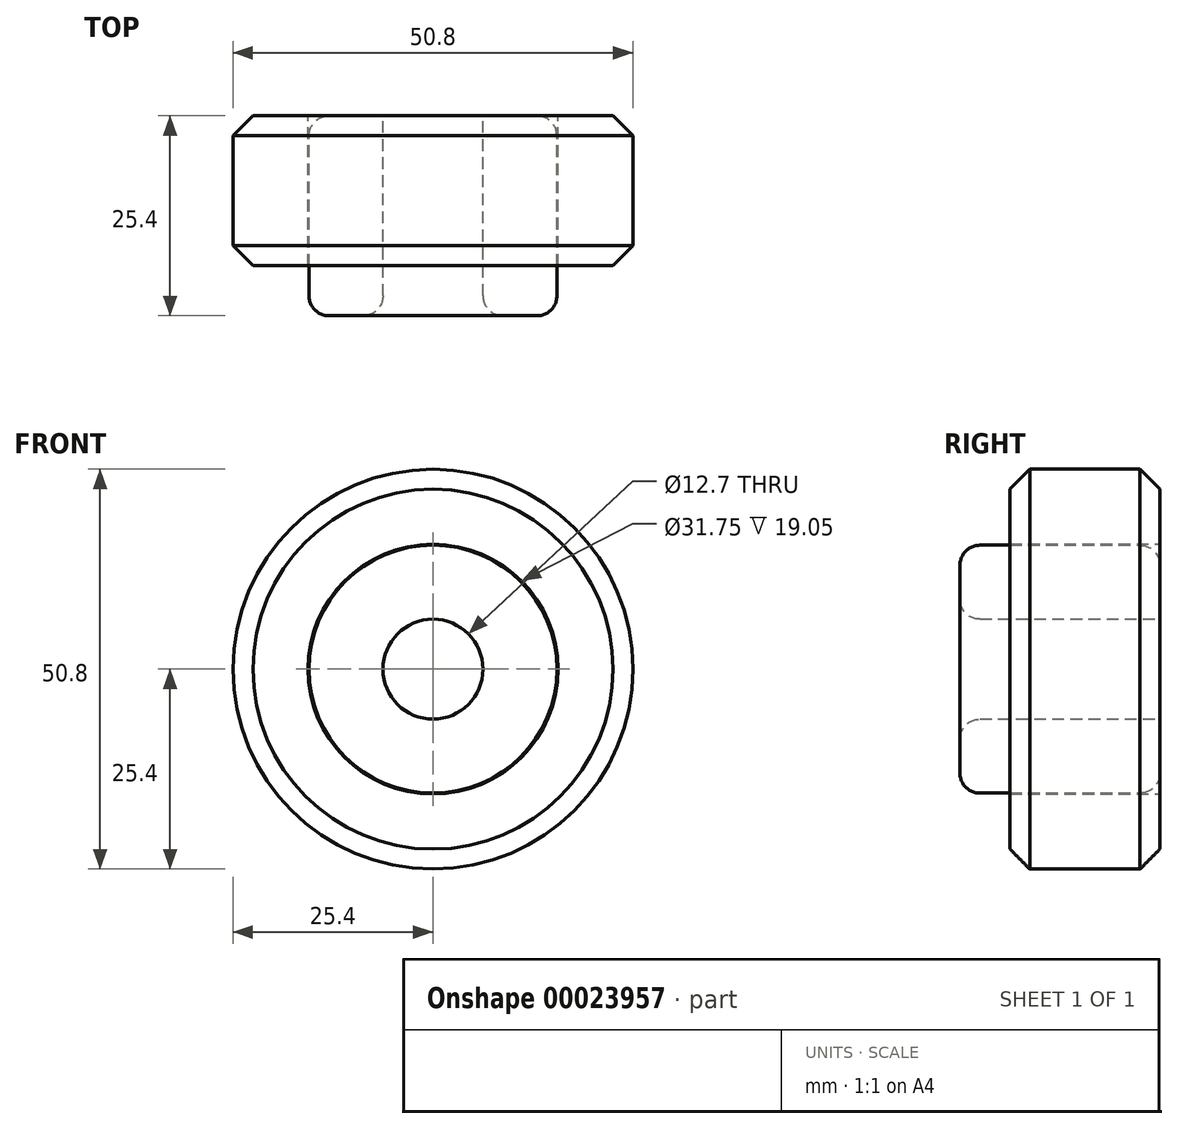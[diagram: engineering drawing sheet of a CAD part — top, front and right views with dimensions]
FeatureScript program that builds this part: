
annotation { "Feature Type Name" : "Feature", "Feature Type Description" : "" }
export const myFeature = defineFeature(function(context is Context, id is Id, definition is map)
    precondition{}
    {
        {
            var Q0;
            Q0=qCreatedBy(makeId("Front.planeOp"),FACE);
            var sketch = newSketch(context, id + "F0", { "sketchPlane" : qUnion([Q0])});
            skCircle(sketch, "E0", {"center": v(0, 0) * mm, "radius": 25.4 * mm});
            skCircle(sketch, "E1", {"center": v(0, 0) * mm, "radius": 15.88 * mm});
            skSolve(sketch);
        }
        {
            var Q0;
            Q0=makeQuery(id+"F0.imprint","IMPRINT",FACE,{"disambiguationData":[TD([[makeQuery(id+"F0.imprint","IMPRINT",EDGE,{"derivedFrom":sQuery(id+"F0.wireOp",EDGE,"E0")}),1.0]])]});
            extrude(context, id + "F1", {"entities" : qUnion([Q0]), "depth" : 19.05 * mm});
        }
        {
            var Q0;
            Q0=makeQuery(id+"F1.opExtrude","SWEPT_FACE",FACE,{"disambiguationData":[OSD([sQuery(id+"F0.wireOp",EDGE,"E0")])]});
            chamfer(context, id + "F2", {"entities" : qUnion([Q0]), "width" : 2.54 * mm, "tangentPropagation" : true});
        }
        {
            var Q0;
            Q0=qCreatedBy(makeId("Front.planeOp"),FACE);
            var sketch = newSketch(context, id + "F3", { "sketchPlane" : qUnion([Q0])});
            skCircle(sketch, "E2", {"center": v(0, 0) * mm, "radius": 15.75 * mm});
            skCircle(sketch, "E3", {"center": v(0, 0) * mm, "radius": 6.35 * mm});
            skSolve(sketch);
        }
        {
            var Q0;
            Q0=makeQuery(id+"F3.imprint","IMPRINT",FACE,{"disambiguationData":[TD([[makeQuery(id+"F3.imprint","IMPRINT",EDGE,{"derivedFrom":sQuery(id+"F3.wireOp",EDGE,"E2")}),1.0]])]});
            extrude(context, id + "F4", {"entities" : qUnion([Q0]), "depth" : 25.4 * mm});
        }
        {
            var Q0;
            Q0=makeQuery(id+"F4.opExtrude","SWEPT_FACE",FACE,{"disambiguationData":[OSD([sQuery(id+"F3.wireOp",EDGE,"E2")])]});
            var Q1;
            Q1=makeQuery(id+"F4.opExtrude","CAP_FACE",FACE,{"disambiguationData":[OSD([sQuery(id+"F3.wireOp",EDGE,"E2"),sQuery(id+"F3.wireOp",EDGE,"E3")])],"isStart":false});
            fillet(context, id + "F5", {"entities" : qUnion([Q0, Q1]), "radius" : 2.54 * mm, "tangentPropagation" : true, "allowEdgeOverflow" : false});
        }
    });
